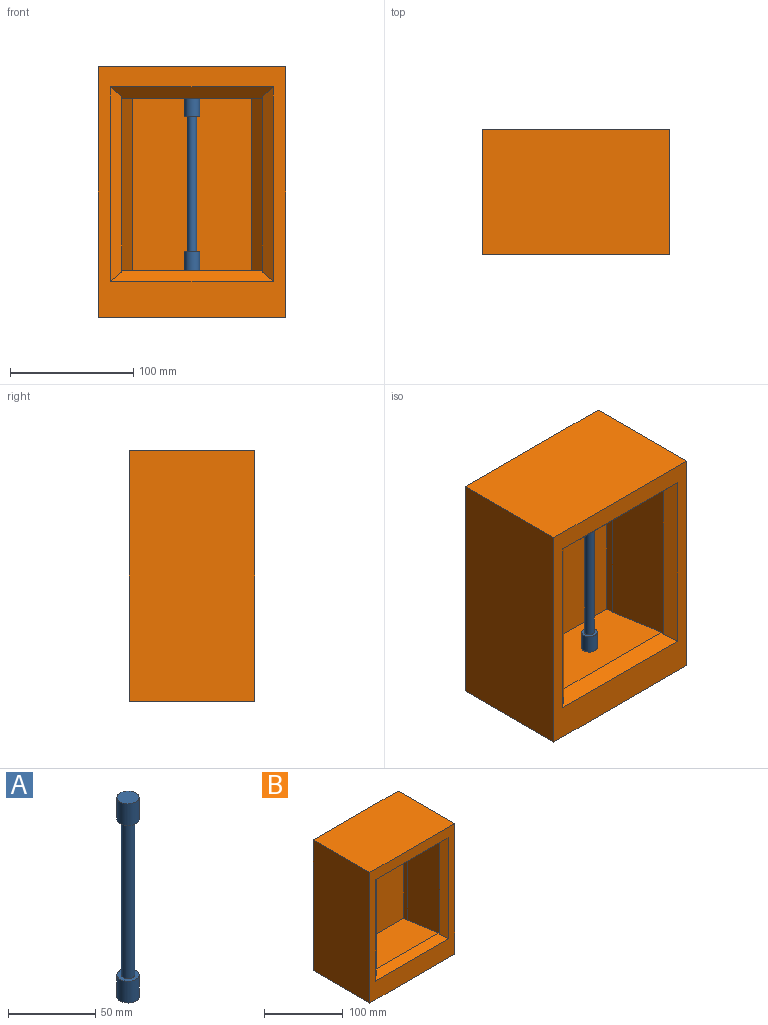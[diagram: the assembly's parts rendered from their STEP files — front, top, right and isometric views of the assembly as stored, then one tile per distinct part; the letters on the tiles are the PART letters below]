
ASSEMBLY  parts=2 mates=1
PART A: 7 faces, bbox 12.7x12.7x139.7 mm
  f0: cylinder r=6.35mm len=15.24mm, axis (0,0,-1), area 608mm2, adj f1,f2
  f1: plane 12.7x12.7mm, normal (0,0,1), area 81.1mm2, adj f0,f3
  f2: plane 12.7x12.7mm, normal (0,0,-1), area 126.7mm2, adj f0
  f3: cylinder r=3.81mm len=109.22mm, axis (0,0,-1), area 2614.6mm2, adj f1,f6
  f4: cylinder r=6.35mm len=15.24mm, axis (0,0,-1), area 608mm2, adj f5,f6
  f5: plane 12.7x12.7mm, normal (0,0,1), area 126.7mm2, adj f4
  f6: plane 12.7x12.7mm, normal (0,0,-1), area 81.1mm2, adj f3,f4
PART B: 17 faces, bbox 152.4x101.6x203.2 mm
  f0: plane 203.2x152.4mm, normal (0,1,0), area 30967.7mm2, adj f1,f3,f4,f9
  f1: plane 203.2x101.6mm, normal (-1,0,0), area 20645.1mm2, adj f0,f2,f4,f9
  f2: plane 203.2x152.4mm, normal (0,-1,0), area 10117.2mm2, adj f1,f3,f4,f9,f13,f14,f15,f16
  f3: plane 203.2x101.6mm, normal (1,0,0), area 20645.1mm2, adj f0,f2,f4,f9
  f4: plane 152.4x101.6mm, normal (0,0,-1), area 15483.8mm2, adj f0,f1,f2,f3
  f5: plane 139.7x5.88mm, normal (-1,0,0), area 821.4mm2, adj f6,f8,f10,f11
  f6: plane 139.7x96.52mm, normal (0,-1,0), area 13483.8mm2, adj f5,f7,f8,f10
  f7: plane 139.7x5.88mm, normal (1,0,0), area 821.4mm2, adj f6,f8,f10,f12
  f8: plane 113.64x54.42mm, normal (0,0,1), area 5667.9mm2, adj f5,f6,f7,f11,f12,f16
  f9: plane 152.4x101.6mm, normal (0,0,1), area 15483.8mm2, adj f0,f1,f2,f3
  f10: plane 113.64x54.42mm, normal (0,0,-1), area 5667.9mm2, adj f5,f6,f7,f11,f12,f13
  f11: plane 142.85x50.12mm, normal (-0.98,-0.17,0), area 7111.7mm2, adj f5,f8,f10,f13,f15,f16
  f12: plane 142.85x50.12mm, normal (0.98,-0.17,0), area 7111.7mm2, adj f7,f8,f10,f13,f14,f16
  f13: plane 132.08x9.08mm, normal (0,-0.71,-0.71), area 1560.8mm2, adj f2,f10,f11,f12,f14,f15
  f14: plane 157.86x8.94mm, normal (0.64,-0.77,0), area 1755.4mm2, adj f2,f12,f13,f16
  f15: plane 157.86x8.94mm, normal (-0.64,-0.77,0), area 1755.4mm2, adj f2,f11,f13,f16
  f16: plane 132.08x9.08mm, normal (0,-0.71,0.71), area 1560.8mm2, adj f2,f8,f11,f12,f14,f15
PLACE A t=(-40.24,37.94,51.24)mm
PLACE B t=(-116.44,2.46,13.14)mm fixed
MATE fastened A.f0 <-> B.f10  axis (0,0,1) through (-40.24,37.94,190.94)mm
